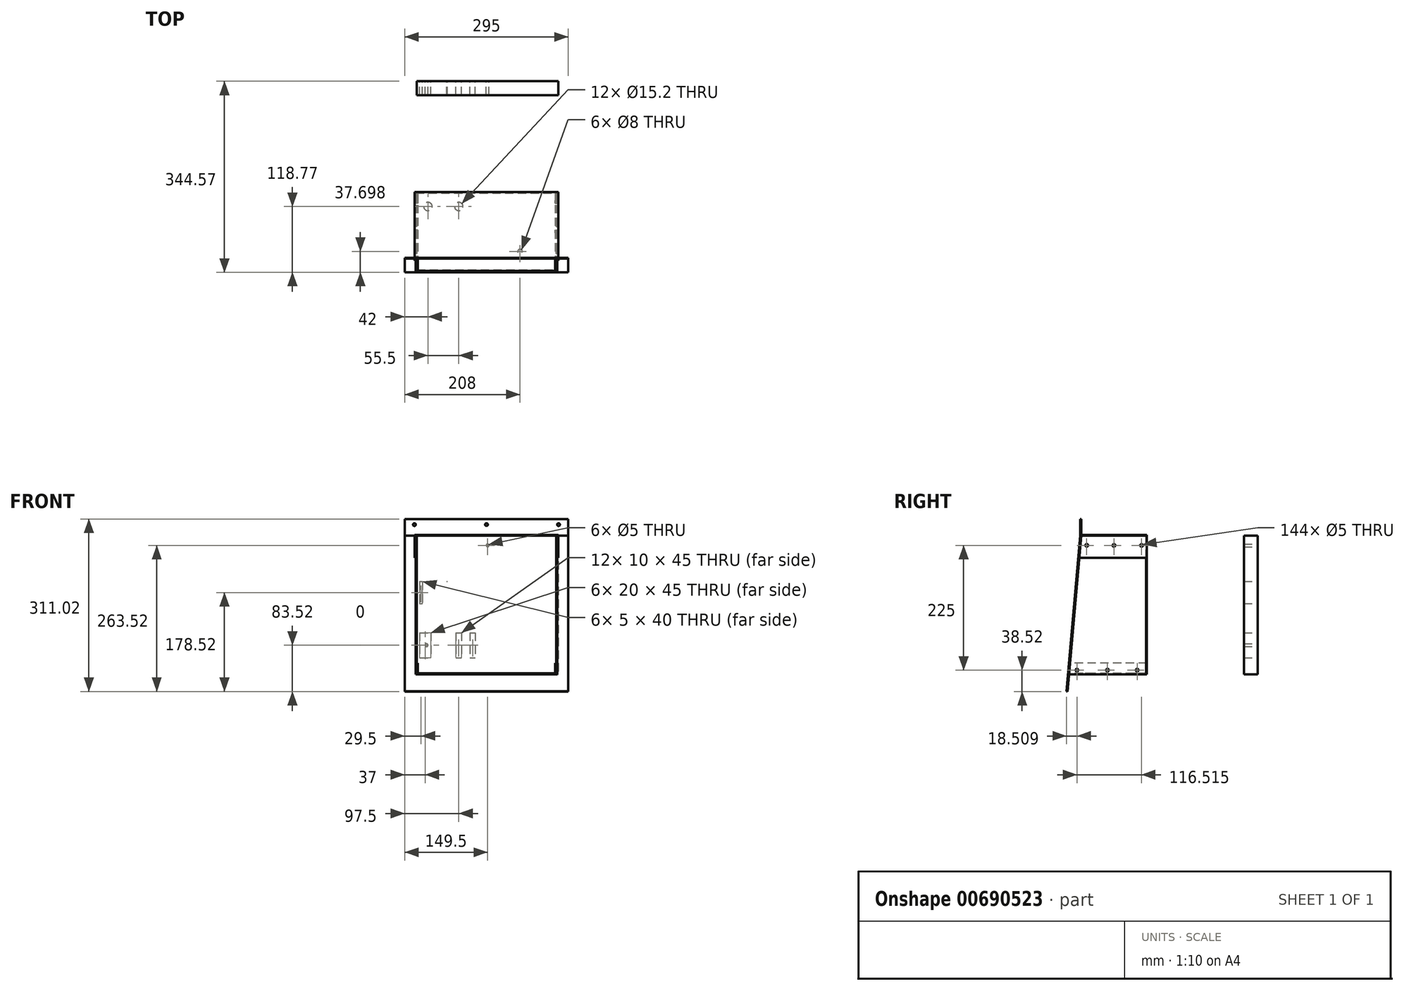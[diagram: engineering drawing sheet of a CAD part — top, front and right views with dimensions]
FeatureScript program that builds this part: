
annotation { "Feature Type Name" : "Feature", "Feature Type Description" : "" }
export const myFeature = defineFeature(function(context is Context, id is Id, definition is map)
    precondition{}
    {
        {
            var Q0;
            Q0=qCreatedBy(makeId("Right.planeOp"),FACE);
            var sketch = newSketch(context, id + "F0", { "sketchPlane" : qUnion([Q0])});
            skLineSegment(sketch, "E0.bottom", {"start": v(0, 0) * mm, "end": v(-141.87, 0) * mm});
            skLineSegment(sketch, "E0.top", {"start": v(0, 250) * mm, "end": v(-120, 250) * mm});
            skLineSegment(sketch, "E0.left", {"start": v(0, 0) * mm, "end": v(0, 250) * mm});
            skLineSegment(sketch, "E0.right", {"start": v(-141.87, 0) * mm, "end": v(-120, 250) * mm});
            skCircle(sketch, "E1", {"center": v(-17.5, 7.5) * mm, "radius": 2.5 * mm});
            skCircle(sketch, "E2", {"center": v(-70.94, 7.5) * mm, "radius": 2.5 * mm});
            skCircle(sketch, "E3", {"center": v(-126.06, 7.5) * mm, "radius": 2.5 * mm});
            skPoint(sketch, "E4", {"position": v(-70.94, 0) * mm});
            skCircle(sketch, "E5", {"center": v(-9.55, 232.5) * mm, "radius": 2.5 * mm});
            skCircle(sketch, "E6", {"center": v(-59.17, 232.5) * mm, "radius": 2.5 * mm});
            skCircle(sketch, "E7", {"center": v(-108.45, 232.5) * mm, "radius": 2.5 * mm});
            skSolve(sketch);
        }
        {
            var Q0;
            Q0 = qSketchRegion(id + "F0", true);
            extrude(context, id + "F1", {"entities" : qUnion([Q0]), "depth" : 1.6 * mm, "offsetDistance" : 25 * mm});
        }
        {
            var Q0;
            Q0=qCreatedBy(makeId("Front.planeOp"),FACE);
            var sketch = newSketch(context, id + "F2", { "sketchPlane" : qUnion([Q0])});
            skLineSegment(sketch, "E8.bottom", {"start": v(0, 0) * mm, "end": v(255, 0) * mm});
            skLineSegment(sketch, "E8.top", {"start": v(0, 250) * mm, "end": v(255, 250) * mm});
            skLineSegment(sketch, "E8.left", {"start": v(0, 0) * mm, "end": v(0, 250) * mm});
            skLineSegment(sketch, "E8.right", {"start": v(255, 0) * mm, "end": v(255, 250) * mm});
            skSolve(sketch);
        }
        {
            var Q0;
            Q0=makeQuery(id+"F2.imprint","IMPRINT",FACE,{"disambiguationData":[TD([[makeQuery(id+"F2.imprint","IMPRINT",EDGE,{"derivedFrom":sQuery(id+"F2.wireOp",EDGE,"E8.bottom")}),1.0]])]});
            var Q1;
            Q1 = qConstructionFilter(qBodyType(qCreatedBy(id + "F2" ,EDGE), BodyType.WIRE), ConstructionObject.NO);
            extrude(context, id + "F3", {"entities" : qUnion([Q0]), "surfaceEntities" : qUnion([Q1]), "depth" : 1.6 * mm, "offsetDistance" : 25 * mm});
        }
        {
            var Q0;
            Q0=qCreatedBy(makeId("Top.planeOp"),FACE);
            var sketch = newSketch(context, id + "F4", { "sketchPlane" : qUnion([Q0])});
            skLineSegment(sketch, "E9.bottom", {"start": v(2, 0) * mm, "end": v(253, 0) * mm});
            skLineSegment(sketch, "E9.top", {"start": v(2, -141.87) * mm, "end": v(253, -141.87) * mm});
            skLineSegment(sketch, "E9.left", {"start": v(2, 0) * mm, "end": v(2, -141.87) * mm});
            skLineSegment(sketch, "E9.right", {"start": v(253, 0) * mm, "end": v(253, -141.87) * mm});
            skCircle(sketch, "E10", {"center": v(22, -25.8) * mm, "radius": 7.6 * mm});
            skCircle(sketch, "E11", {"center": v(77.5, -25.8) * mm, "radius": 7.6 * mm});
            skCircle(sketch, "E12", {"center": v(188, -106.87) * mm, "radius": 4 * mm});
            skSolve(sketch);
        }
        {
            var Q0;
            Q0 = qSketchRegion(id + "F4", true);
            extrude(context, id + "F5", {"entities" : qUnion([Q0]), "depth" : 1.6 * mm, "offsetDistance" : 25 * mm});
        }
        {
            var Q0;
            Q0=sQuery(id+"F0.wireOp",EDGE,"E0.top");
            cPlane(context, id + "F6", {"entities" : qUnion([Q0]), "cplaneType" : CPlaneType.LINE_ANGLE, "offset" : 25 * mm, "angle" : 0 * degree, "width" : 150 * mm, "height" : 150 * mm});
        }
        {
            var Q0;
            Q0=qCreatedBy(id+"F6.planeOp",FACE);
            var sketch = newSketch(context, id + "F7", { "sketchPlane" : qUnion([Q0])});
            skLineSegment(sketch, "E13.bottom", {"start": v(-2, 0) * mm, "end": v(257, 0) * mm});
            skLineSegment(sketch, "E13.top", {"start": v(-2, 120) * mm, "end": v(257, 120) * mm});
            skLineSegment(sketch, "E13.left", {"start": v(-2, 0) * mm, "end": v(-2, 120) * mm});
            skLineSegment(sketch, "E13.right", {"start": v(257, 0) * mm, "end": v(257, 120) * mm});
            skSolve(sketch);
        }
        {
            var Q0;
            Q0 = qSketchRegion(id + "F7", true);
            extrude(context, id + "F8", {"entities" : qUnion([Q0]), "oppositeDirection" : true, "depth" : 1.6 * mm, "offsetDistance" : 25 * mm});
        }
        {
            var Q0;
            Q0=sQuery(id+"F2.wireOp",EDGE,"E8.right");
            cPlane(context, id + "F9", {"entities" : qUnion([Q0]), "cplaneType" : CPlaneType.LINE_ANGLE, "offset" : 25 * mm, "angle" : 0 * degree, "width" : 150 * mm, "height" : 150 * mm});
        }
        {
            var Q0;
            Q0=qCreatedBy(id+"F9.planeOp",FACE);
            var sketch = newSketch(context, id + "F10", { "sketchPlane" : qUnion([Q0])});
            skLineSegment(sketch, "E14.bottom", {"start": v(0, 0) * mm, "end": v(-141.87, 0) * mm});
            skLineSegment(sketch, "E14.top", {"start": v(0, 250) * mm, "end": v(-120, 250) * mm});
            skLineSegment(sketch, "E14.left", {"start": v(0, 0) * mm, "end": v(0, 250) * mm});
            skLineSegment(sketch, "E14.right", {"start": v(-141.87, 0) * mm, "end": v(-120, 250) * mm});
            skCircle(sketch, "E15", {"center": v(-126.06, 7.5) * mm, "radius": 2.5 * mm});
            skCircle(sketch, "E16", {"center": v(-70.94, 7.5) * mm, "radius": 2.5 * mm});
            skCircle(sketch, "E17", {"center": v(-17.5, 7.5) * mm, "radius": 2.5 * mm});
            skCircle(sketch, "E18", {"center": v(-9.55, 232.5) * mm, "radius": 2.5 * mm});
            skCircle(sketch, "E19", {"center": v(-59.17, 232.5) * mm, "radius": 2.5 * mm});
            skCircle(sketch, "E20", {"center": v(-108.45, 232.5) * mm, "radius": 2.5 * mm});
            skLineSegment(sketch, "E21", {"start": v(-141.87, 0) * mm, "end": v(-141.87, -30) * mm});
            skSolve(sketch);
        }
        {
            var Q0;
            Q0 = qSketchRegion(id + "F10", true);
            extrude(context, id + "F11", {"entities" : qUnion([Q0]), "oppositeDirection" : true, "depth" : 1.6 * mm, "offsetDistance" : 25 * mm});
        }
        {
            var Q0;
            Q0=sQuery(id+"F4.wireOp",EDGE,"E9.left");
            cPlane(context, id + "F12", {"entities" : qUnion([Q0]), "cplaneType" : CPlaneType.LINE_ANGLE, "offset" : 25 * mm, "angle" : 90 * degree, "width" : 150 * mm, "height" : 150 * mm});
        }
        {
            var Q0;
            Q0=qCreatedBy(id+"F12.planeOp",FACE);
            var sketch = newSketch(context, id + "F13", { "sketchPlane" : qUnion([Q0])});
            skLineSegment(sketch, "E22.bottom", {"start": v(0, 0) * mm, "end": v(-141.87, 0) * mm});
            skLineSegment(sketch, "E22.top", {"start": v(0, 20) * mm, "end": v(-140.12, 20) * mm});
            skLineSegment(sketch, "E22.left", {"start": v(0, 0) * mm, "end": v(0, 20) * mm});
            skLineSegment(sketch, "E22.right", {"start": v(-141.87, 0) * mm, "end": v(-140.12, 20) * mm});
            skCircle(sketch, "E23", {"center": v(-126.06, 7.5) * mm, "radius": 2.5 * mm});
            skCircle(sketch, "E24", {"center": v(-70.94, 7.5) * mm, "radius": 2.5 * mm});
            skCircle(sketch, "E25", {"center": v(-17.5, 7.5) * mm, "radius": 2.5 * mm});
            skPoint(sketch, "E26", {"position": v(-87.8, 0) * mm});
            skSolve(sketch);
        }
        {
            var Q0;
            Q0 = qSketchRegion(id + "F13", true);
            extrude(context, id + "F14", {"entities" : qUnion([Q0]), "depth" : 1.6 * mm, "offsetDistance" : 25 * mm});
        }
        {
            var Q0;
            Q0=sQuery(id+"F7.wireOp",EDGE,"E13.left");
            cPlane(context, id + "F15", {"entities" : qUnion([Q0]), "cplaneType" : CPlaneType.LINE_ANGLE, "offset" : 25 * mm, "angle" : 90 * degree, "width" : 150 * mm, "height" : 150 * mm});
        }
        {
            var Q0;
            Q0=qCreatedBy(id+"F15.planeOp",FACE);
            var sketch = newSketch(context, id + "F16", { "sketchPlane" : qUnion([Q0])});
            skLineSegment(sketch, "E27.bottom", {"start": v(0, 250) * mm, "end": v(-120, 250) * mm});
            skLineSegment(sketch, "E27.top", {"start": v(0, 210) * mm, "end": v(-123.5, 210) * mm});
            skLineSegment(sketch, "E27.left", {"start": v(0, 250) * mm, "end": v(0, 210) * mm});
            skLineSegment(sketch, "E27.right", {"start": v(-120, 250) * mm, "end": v(-123.5, 210) * mm});
            skCircle(sketch, "E28", {"center": v(-9.55, 232.5) * mm, "radius": 2.5 * mm});
            skCircle(sketch, "E29", {"center": v(-59.17, 232.5) * mm, "radius": 2.5 * mm});
            skCircle(sketch, "E30", {"center": v(-108.45, 232.5) * mm, "radius": 2.5 * mm});
            skSolve(sketch);
        }
        {
            var Q0;
            Q0 = qSketchRegion(id + "F16", true);
            extrude(context, id + "F17", {"entities" : qUnion([Q0]), "depth" : 1.6 * mm, "offsetDistance" : 25 * mm});
        }
        {
            var Q0;
            Q0=sQuery(id+"F7.wireOp",EDGE,"E13.right");
            cPlane(context, id + "F18", {"entities" : qUnion([Q0]), "cplaneType" : CPlaneType.LINE_ANGLE, "offset" : 25 * mm, "angle" : 90 * degree, "width" : 150 * mm, "height" : 150 * mm});
        }
        {
            var Q0;
            Q0=qCreatedBy(id+"F18.planeOp",FACE);
            var sketch = newSketch(context, id + "F19", { "sketchPlane" : qUnion([Q0])});
            skLineSegment(sketch, "E31.bottom", {"start": v(0, 250) * mm, "end": v(-120, 250) * mm});
            skLineSegment(sketch, "E31.top", {"start": v(0, 210) * mm, "end": v(-123.5, 210) * mm});
            skLineSegment(sketch, "E31.left", {"start": v(0, 250) * mm, "end": v(0, 210) * mm});
            skLineSegment(sketch, "E31.right", {"start": v(-120, 250) * mm, "end": v(-123.5, 210) * mm});
            skCircle(sketch, "E32", {"center": v(-108.45, 232.5) * mm, "radius": 2.5 * mm});
            skCircle(sketch, "E33", {"center": v(-59.17, 232.5) * mm, "radius": 2.5 * mm});
            skCircle(sketch, "E34", {"center": v(-9.55, 232.5) * mm, "radius": 2.5 * mm});
            skSolve(sketch);
        }
        {
            var Q0;
            Q0 = qSketchRegion(id + "F19", true);
            extrude(context, id + "F20", {"entities" : qUnion([Q0]), "oppositeDirection" : true, "depth" : 1.6 * mm, "offsetDistance" : 25 * mm});
        }
        {
            var Q0;
            Q0=sQuery(id+"F4.wireOp",EDGE,"E9.right");
            cPlane(context, id + "F21", {"entities" : qUnion([Q0]), "cplaneType" : CPlaneType.LINE_ANGLE, "offset" : 25 * mm, "angle" : 90 * degree, "width" : 150 * mm, "height" : 150 * mm});
        }
        {
            var Q0;
            Q0=qCreatedBy(id+"F21.planeOp",FACE);
            var sketch = newSketch(context, id + "F22", { "sketchPlane" : qUnion([Q0])});
            skLineSegment(sketch, "E35.bottom", {"start": v(0, 0) * mm, "end": v(-141.87, 0) * mm});
            skLineSegment(sketch, "E35.top", {"start": v(0, 20) * mm, "end": v(-140.12, 20) * mm});
            skLineSegment(sketch, "E35.left", {"start": v(0, 0) * mm, "end": v(0, 20) * mm});
            skLineSegment(sketch, "E35.right", {"start": v(-141.87, 0) * mm, "end": v(-140.12, 20) * mm});
            skCircle(sketch, "E36", {"center": v(-17.5, 7.5) * mm, "radius": 2.5 * mm});
            skCircle(sketch, "E37", {"center": v(-70.94, 7.5) * mm, "radius": 2.5 * mm});
            skCircle(sketch, "E38", {"center": v(-126.06, 7.5) * mm, "radius": 2.5 * mm});
            skSolve(sketch);
        }
        {
            var Q0;
            Q0 = qSketchRegion(id + "F22", true);
            extrude(context, id + "F23", {"entities" : qUnion([Q0]), "oppositeDirection" : true, "depth" : 1.6 * mm, "offsetDistance" : 25 * mm});
        }
        {
            var Q0;
            Q0=sQuery(id+"F0.wireOp",EDGE,"E0.right");
            cPlane(context, id + "F24", {"entities" : qUnion([Q0]), "cplaneType" : CPlaneType.LINE_ANGLE, "offset" : 25 * mm, "angle" : 90 * degree, "width" : 150 * mm, "height" : 150 * mm});
        }
        {
            var Q0;
            Q0=qCreatedBy(id+"F24.planeOp",FACE);
            var sketch = newSketch(context, id + "F25", { "sketchPlane" : qUnion([Q0])});
            skLineSegment(sketch, "E39.bottom", {"start": v(0, 238.59) * mm, "end": v(-255, 238.59) * mm});
            skLineSegment(sketch, "E39.top", {"start": v(0, -12.36) * mm, "end": v(-255, -12.36) * mm});
            skLineSegment(sketch, "E39.left", {"start": v(0, 238.59) * mm, "end": v(0, -12.36) * mm});
            skLineSegment(sketch, "E39.right", {"start": v(-255, 238.59) * mm, "end": v(-255, -12.36) * mm});
            skLineSegment(sketch, "E40.bottom", {"start": v(20, 238.59) * mm, "end": v(-275, 238.59) * mm});
            skLineSegment(sketch, "E40.top", {"start": v(20, -43.36) * mm, "end": v(-275, -43.36) * mm});
            skLineSegment(sketch, "E40.left", {"start": v(20, 238.59) * mm, "end": v(20, -43.36) * mm});
            skLineSegment(sketch, "E40.right", {"start": v(-275, 238.59) * mm, "end": v(-275, -43.36) * mm});
            skSolve(sketch);
        }
        {
            var Q0;
            Q0=makeQuery(id+"F2.imprint","IMPRINT",FACE,{"disambiguationData":[TD([[makeQuery(id+"F2.imprint","IMPRINT",EDGE,{"derivedFrom":sQuery(id+"F2.wireOp",EDGE,"E8.bottom")}),1.0]])]});
            cPlane(context, id + "F26", {"entities" : qUnion([Q0]), "cplaneType" : CPlaneType.OFFSET, "offset" : 200 * mm, "oppositeDirection" : true, "width" : 150 * mm, "height" : 150 * mm});
        }
        {
            var Q0;
            Q0=qCreatedBy(id+"F26.planeOp",FACE);
            var sketch = newSketch(context, id + "F27", { "sketchPlane" : qUnion([Q0])});
            skLineSegment(sketch, "E41.bottom", {"start": v(2, 250) * mm, "end": v(257, 250) * mm});
            skLineSegment(sketch, "E41.top", {"start": v(2, 0) * mm, "end": v(257, 0) * mm});
            skLineSegment(sketch, "E41.left", {"start": v(2, 250) * mm, "end": v(2, 0) * mm});
            skLineSegment(sketch, "E41.right", {"start": v(257, 250) * mm, "end": v(257, 0) * mm});
            skLineSegment(sketch, "E42.bottom", {"start": v(7, 245) * mm, "end": v(252, 245) * mm});
            skLineSegment(sketch, "E42.top", {"start": v(7, 5) * mm, "end": v(252, 5) * mm});
            skLineSegment(sketch, "E42.left", {"start": v(7, 245) * mm, "end": v(7, 5) * mm});
            skLineSegment(sketch, "E42.right", {"start": v(252, 245) * mm, "end": v(252, 5) * mm});
            skCircle(sketch, "E43", {"center": v(14.5, 12.5) * mm, "radius": 2.5 * mm});
            skCircle(sketch, "E44", {"center": v(129.5, 232.5) * mm, "radius": 2.5 * mm});
            skLineSegment(sketch, "E45.bottom", {"start": v(7, 75) * mm, "end": v(122.5, 75) * mm});
            skLineSegment(sketch, "E45.top", {"start": v(7, 30) * mm, "end": v(122.5, 30) * mm});
            skLineSegment(sketch, "E45.left", {"start": v(7, 75) * mm, "end": v(7, 30) * mm});
            skLineSegment(sketch, "E45.right", {"start": v(122.5, 75) * mm, "end": v(122.5, 30) * mm});
            skLineSegment(sketch, "E46.bottom", {"start": v(7, 167.5) * mm, "end": v(103, 167.5) * mm});
            skLineSegment(sketch, "E46.top", {"start": v(7, 127.5) * mm, "end": v(103, 127.5) * mm});
            skLineSegment(sketch, "E46.left", {"start": v(7, 167.5) * mm, "end": v(7, 127.5) * mm});
            skLineSegment(sketch, "E46.right", {"start": v(103, 167.5) * mm, "end": v(103, 127.5) * mm});
            skLineSegment(sketch, "E47.bottom", {"start": v(12, 190) * mm, "end": v(32, 190) * mm});
            skLineSegment(sketch, "E47.top", {"start": v(12, 105) * mm, "end": v(32, 105) * mm});
            skLineSegment(sketch, "E47.left", {"start": v(12, 190) * mm, "end": v(12, 105) * mm});
            skLineSegment(sketch, "E47.right", {"start": v(32, 190) * mm, "end": v(32, 105) * mm});
            skLineSegment(sketch, "E48.bottom", {"start": v(52, 196) * mm, "end": v(103, 196) * mm});
            skLineSegment(sketch, "E48.top", {"start": v(52, 105) * mm, "end": v(103, 105) * mm});
            skLineSegment(sketch, "E48.left", {"start": v(52, 196) * mm, "end": v(52, 105) * mm});
            skLineSegment(sketch, "E48.right", {"start": v(103, 196) * mm, "end": v(103, 105) * mm});
            skPoint(sketch, "E49", {"position": v(7, 52.5) * mm});
            skCircle(sketch, "E50", {"center": v(14.5, 147.5) * mm, "radius": 2.5 * mm});
            skPoint(sketch, "E51", {"position": v(7, 147.5) * mm});
            skLineSegment(sketch, "E52.bottom", {"start": v(152, 245) * mm, "end": v(252, 245) * mm});
            skLineSegment(sketch, "E52.top", {"start": v(152, 85) * mm, "end": v(252, 85) * mm});
            skLineSegment(sketch, "E52.left", {"start": v(152, 245) * mm, "end": v(152, 85) * mm});
            skLineSegment(sketch, "E52.right", {"start": v(252, 245) * mm, "end": v(252, 85) * mm});
            skCircle(sketch, "E53", {"center": v(202, 240) * mm, "radius": 2.5 * mm});
            skCircle(sketch, "E54", {"center": v(202, 90) * mm, "radius": 2.5 * mm});
            skPoint(sketch, "E55", {"position": v(202, 245) * mm});
            skLineSegment(sketch, "E56.bottom", {"start": v(56.85, 169.8) * mm, "end": v(98.15, 169.8) * mm});
            skLineSegment(sketch, "E56.top", {"start": v(56.85, 131.2) * mm, "end": v(98.15, 131.2) * mm});
            skLineSegment(sketch, "E56.left", {"start": v(56.85, 169.8) * mm, "end": v(56.85, 131.2) * mm});
            skLineSegment(sketch, "E56.right", {"start": v(98.15, 169.8) * mm, "end": v(98.15, 131.2) * mm});
            skPoint(sketch, "E57", {"position": v(77.5, 196) * mm});
            skPoint(sketch, "E58", {"position": v(77.5, 169.8) * mm});
            skPoint(sketch, "E59", {"position": v(98.15, 150.5) * mm});
            skPoint(sketch, "E60", {"position": v(103, 150.5) * mm});
            skCircle(sketch, "E61", {"center": v(56.85, 169.8) * mm, "radius": 2.5 * mm});
            skCircle(sketch, "E62", {"center": v(98.15, 169.8) * mm, "radius": 2.5 * mm});
            skCircle(sketch, "E63", {"center": v(98.15, 131.2) * mm, "radius": 2.5 * mm});
            skCircle(sketch, "E64", {"center": v(56.85, 131.2) * mm, "radius": 2.5 * mm});
            skLineSegment(sketch, "E65.bottom", {"start": v(17, 75) * mm, "end": v(27, 75) * mm});
            skLineSegment(sketch, "E65.top", {"start": v(17, 30) * mm, "end": v(27, 30) * mm});
            skLineSegment(sketch, "E65.left", {"start": v(17, 75) * mm, "end": v(17, 30) * mm});
            skLineSegment(sketch, "E65.right", {"start": v(27, 75) * mm, "end": v(27, 30) * mm});
            skPoint(sketch, "E66", {"position": v(22, 75) * mm});
            skPoint(sketch, "E67", {"position": v(22, 105) * mm});
            skPoint(sketch, "E68", {"position": v(12, 147.5) * mm});
            skPoint(sketch, "E69", {"position": v(77.5, 105) * mm});
            skLineSegment(sketch, "E70.bottom", {"start": v(72.5, 75) * mm, "end": v(82.5, 75) * mm});
            skLineSegment(sketch, "E70.top", {"start": v(72.5, 30) * mm, "end": v(82.5, 30) * mm});
            skLineSegment(sketch, "E70.left", {"start": v(72.5, 75) * mm, "end": v(72.5, 30) * mm});
            skLineSegment(sketch, "E70.right", {"start": v(82.5, 75) * mm, "end": v(82.5, 30) * mm});
            skPoint(sketch, "E71", {"position": v(77.5, 75) * mm});
            skLineSegment(sketch, "E72.bottom", {"start": v(97.5, 75) * mm, "end": v(107.5, 75) * mm});
            skLineSegment(sketch, "E72.top", {"start": v(97.5, 30) * mm, "end": v(107.5, 30) * mm});
            skLineSegment(sketch, "E72.left", {"start": v(97.5, 75) * mm, "end": v(97.5, 30) * mm});
            skLineSegment(sketch, "E72.right", {"start": v(107.5, 75) * mm, "end": v(107.5, 30) * mm});
            skPoint(sketch, "E73", {"position": v(32, 147.5) * mm});
            skCircle(sketch, "E74", {"center": v(34.5, 147.5) * mm, "radius": 2.5 * mm});
            skCircle(sketch, "E75", {"center": v(90.5, 147.5) * mm, "radius": 2.5 * mm});
            skCircle(sketch, "E76", {"center": v(19.5, 52.5) * mm, "radius": 2.5 * mm});
            skCircle(sketch, "E77", {"center": v(110, 52.5) * mm, "radius": 2.5 * mm});
            skCircle(sketch, "E78", {"center": v(14.5, 232.5) * mm, "radius": 2.5 * mm});
            skCircle(sketch, "E79", {"center": v(239.5, 12.5) * mm, "radius": 2.5 * mm});
            skSolve(sketch);
        }
        {
            var Q0;
            {var subQ0=sQuery(id+"F27.wireOp",EDGE,"E74");Q0=makeQuery(id+"F27.imprint","IMPRINT",FACE,{"disambiguationData":[TD([[makeQuery(id+"F27.imprint","IMPRINT",EDGE,{"derivedFrom":subQ0}),-1.0]])]});}
            var Q1;
            {var subQ0=sQuery(id+"F27.wireOp",EDGE,"E65.right");Q1=makeQuery(id+"F27.imprint","IMPRINT",FACE,{"disambiguationData":[TD([[makeQuery(id+"F27.imprint","IMPRINT",EDGE,{"derivedFrom":subQ0}),1.0]])]});}
            var Q2;
            {var subQ0=sQuery(id+"F27.wireOp",EDGE,"E70.right");Q2=makeQuery(id+"F27.imprint","IMPRINT",FACE,{"disambiguationData":[TD([[makeQuery(id+"F27.imprint","IMPRINT",EDGE,{"derivedFrom":subQ0}),1.0]])]});}
            var Q3;
            Q3=makeQuery(id+"F27.imprint","IMPRINT",FACE,{"disambiguationData":[TD([[makeQuery(id+"F27.imprint","IMPRINT",EDGE,{"derivedFrom":sQuery(id+"F27.wireOp",EDGE,"E52.bottom")}),-1.0]])]});
            var Q4;
            {var subQ5=sQuery(id+"F27.wireOp",EDGE,"E48.top");Q4=makeQuery(id+"F27.imprint","IMPRINT",FACE,{"disambiguationData":[TD([[makeQuery(id+"F27.imprint","IMPRINT",EDGE,{"derivedFrom":subQ5}),1.0]])]});}
            var Q5;
            {var subQ1=sQuery(id+"F27.wireOp",EDGE,"E48.bottom");Q5=makeQuery(id+"F27.imprint","IMPRINT",FACE,{"disambiguationData":[TD([[makeQuery(id+"F27.imprint","IMPRINT",EDGE,{"derivedFrom":subQ1}),-1.0]])]});}
            var Q6;
            {var subQ5=sQuery(id+"F27.wireOp",EDGE,"E47.bottom");Q6=makeQuery(id+"F27.imprint","IMPRINT",FACE,{"disambiguationData":[TD([[makeQuery(id+"F27.imprint","IMPRINT",EDGE,{"derivedFrom":subQ5}),-1.0]])]});}
            var Q7;
            {var subQ5=sQuery(id+"F27.wireOp",EDGE,"E47.top");Q7=makeQuery(id+"F27.imprint","IMPRINT",FACE,{"disambiguationData":[TD([[makeQuery(id+"F27.imprint","IMPRINT",EDGE,{"derivedFrom":subQ5}),1.0]])]});}
            var Q8;
            Q8=makeQuery(id+"F27.imprint","IMPRINT",FACE,{"disambiguationData":[TD([[makeQuery(id+"F27.imprint","IMPRINT",EDGE,{"derivedFrom":sQuery(id+"F27.wireOp",EDGE,"E75")}),-1.0]])]});
            var Q9;
            Q9=makeQuery(id+"F27.imprint","IMPRINT",FACE,{"disambiguationData":[TD([[makeQuery(id+"F27.imprint","IMPRINT",EDGE,{"derivedFrom":sQuery(id+"F27.wireOp",EDGE,"E70.bottom")}),-1.0]])]});
            var Q10;
            {var subQ33=sQuery(id+"F27.wireOp",EDGE,"E42.bottom");Q10=makeQuery(id+"F27.imprint","IMPRINT",FACE,{"disambiguationData":[TD([[makeQuery(id+"F27.imprint","IMPRINT",EDGE,{"derivedFrom":subQ33}),-1.0]])]});}
            var Q11;
            {var subQ1=sQuery(id+"F27.wireOp",EDGE,"E72.bottom");Q11=makeQuery(id+"F27.imprint","IMPRINT",FACE,{"disambiguationData":[TD([[makeQuery(id+"F27.imprint","IMPRINT",EDGE,{"derivedFrom":subQ1}),-1.0]])]});}
            var Q12;
            Q12=makeQuery(id+"F27.imprint","IMPRINT",FACE,{"disambiguationData":[TD([[makeQuery(id+"F27.imprint","IMPRINT",EDGE,{"derivedFrom":sQuery(id+"F27.wireOp",EDGE,"E41.bottom")}),-1.0]])]});
            var Q13;
            {var subQ4=sQuery(id+"F27.wireOp",EDGE,"E45.left");Q13=makeQuery(id+"F27.imprint","IMPRINT",FACE,{"disambiguationData":[TD([[makeQuery(id+"F27.imprint","IMPRINT",EDGE,{"derivedFrom":subQ4}),1.0]])]});}
            var Q14;
            {var subQ0=sQuery(id+"F27.wireOp",EDGE,"E61");var subQ1=sQuery(id+"F27.wireOp",EDGE,"E46.bottom");var subQ2=makeQuery(id+"F27.imprint","INTERSECT",VERTEX,{"disambiguationData":[OD(1.0)],"derivedFrom":[subQ1,subQ0]});Q14=makeQuery(id+"F27.imprint","IMPRINT",FACE,{"disambiguationData":[TD([[makeQuery(id+"F27.imprint","IMPRINT",EDGE,{"disambiguationData":[TD([[subQ2,-1.0]])],"derivedFrom":subQ1}),1.0]])]});}
            var Q15;
            {var subQ0=sQuery(id+"F27.wireOp",EDGE,"E45.right");Q15=makeQuery(id+"F27.imprint","IMPRINT",FACE,{"disambiguationData":[TD([[makeQuery(id+"F27.imprint","IMPRINT",EDGE,{"derivedFrom":subQ0}),-1.0]])]});}
            var Q16;
            {var subQ0=sQuery(id+"F27.wireOp",EDGE,"E50");Q16=makeQuery(id+"F27.imprint","IMPRINT",FACE,{"disambiguationData":[TD([[makeQuery(id+"F27.imprint","IMPRINT",EDGE,{"derivedFrom":subQ0}),-1.0]])]});}
            var Q17;
            {var subQ1=sQuery(id+"F27.wireOp",EDGE,"E46.bottom");var subQ18=sQuery(id+"F27.wireOp",EDGE,"E48.left");var subQ19=makeQuery(id+"F27.imprint","INTERSECT",VERTEX,{"derivedFrom":[subQ1,subQ18]});Q17=makeQuery(id+"F27.imprint","IMPRINT",FACE,{"disambiguationData":[TD([[makeQuery(id+"F27.imprint","IMPRINT",EDGE,{"disambiguationData":[TD([[subQ19,-1.0]])],"derivedFrom":subQ1}),-1.0]])]});}
            var Q18;
            {var subQ4=sQuery(id+"F27.wireOp",EDGE,"E65.bottom");Q18=makeQuery(id+"F27.imprint","IMPRINT",FACE,{"disambiguationData":[TD([[makeQuery(id+"F27.imprint","IMPRINT",EDGE,{"derivedFrom":subQ4}),-1.0]])]});}
            var Q19;
            {var subQ4=sQuery(id+"F27.wireOp",EDGE,"E46.left");Q19=makeQuery(id+"F27.imprint","IMPRINT",FACE,{"disambiguationData":[TD([[makeQuery(id+"F27.imprint","IMPRINT",EDGE,{"derivedFrom":subQ4}),1.0]])]});}
            var Q20;
            Q20=makeQuery(id+"F27.imprint","IMPRINT",FACE,{"disambiguationData":[TD([[makeQuery(id+"F27.imprint","IMPRINT",EDGE,{"derivedFrom":sQuery(id+"F27.wireOp",EDGE,"E44")}),-1.0]])]});
            var Q21;
            Q21=makeQuery(id+"F27.imprint","IMPRINT",FACE,{"disambiguationData":[TD([[makeQuery(id+"F27.imprint","IMPRINT",EDGE,{"derivedFrom":sQuery(id+"F27.wireOp",EDGE,"E54")}),1.0]])]});
            var Q22;
            Q22=makeQuery(id+"F27.imprint","IMPRINT",FACE,{"disambiguationData":[TD([[makeQuery(id+"F27.imprint","IMPRINT",EDGE,{"derivedFrom":sQuery(id+"F27.wireOp",EDGE,"E77")}),1.0]])]});
            var Q23;
            Q23=makeQuery(id+"F27.imprint","IMPRINT",FACE,{"disambiguationData":[TD([[makeQuery(id+"F27.imprint","IMPRINT",EDGE,{"derivedFrom":sQuery(id+"F27.wireOp",EDGE,"E78")}),1.0]])]});
            var Q24;
            Q24=makeQuery(id+"F27.imprint","IMPRINT",FACE,{"disambiguationData":[TD([[makeQuery(id+"F27.imprint","IMPRINT",EDGE,{"derivedFrom":sQuery(id+"F27.wireOp",EDGE,"E79")}),1.0]])]});
            var Q25;
            Q25=makeQuery(id+"F27.imprint","IMPRINT",FACE,{"disambiguationData":[TD([[makeQuery(id+"F27.imprint","IMPRINT",EDGE,{"derivedFrom":sQuery(id+"F27.wireOp",EDGE,"E43")}),1.0]])]});
            var Q26;
            Q26=makeQuery(id+"F27.imprint","IMPRINT",FACE,{"disambiguationData":[TD([[makeQuery(id+"F27.imprint","IMPRINT",EDGE,{"derivedFrom":sQuery(id+"F27.wireOp",EDGE,"E50")}),1.0]])]});
            var Q27;
            Q27=makeQuery(id+"F27.imprint","IMPRINT",FACE,{"disambiguationData":[TD([[makeQuery(id+"F27.imprint","IMPRINT",EDGE,{"derivedFrom":sQuery(id+"F27.wireOp",EDGE,"E53")}),1.0]])]});
            var Q28;
            Q28=makeQuery(id+"F27.imprint","IMPRINT",FACE,{"disambiguationData":[TD([[makeQuery(id+"F27.imprint","IMPRINT",EDGE,{"derivedFrom":sQuery(id+"F27.wireOp",EDGE,"E74")}),1.0]])]});
            var Q29;
            Q29=makeQuery(id+"F27.imprint","IMPRINT",FACE,{"disambiguationData":[TD([[makeQuery(id+"F27.imprint","IMPRINT",EDGE,{"derivedFrom":sQuery(id+"F27.wireOp",EDGE,"E75")}),1.0]])]});
            var Q30;
            Q30=makeQuery(id+"F27.imprint","IMPRINT",FACE,{"disambiguationData":[TD([[makeQuery(id+"F27.imprint","IMPRINT",EDGE,{"derivedFrom":sQuery(id+"F27.wireOp",EDGE,"E76")}),1.0]])]});
            var Q31;
            {var subQ0=sQuery(id+"F27.wireOp",EDGE,"E56.right");var subQ1=sQuery(id+"F27.wireOp",EDGE,"E56.top");var subQ2=makeQuery(id+"F27.imprint","INTERSECT",VERTEX,{"derivedFrom":[subQ1,subQ0]});Q31=makeQuery(id+"F27.imprint","IMPRINT",FACE,{"disambiguationData":[TD([[makeQuery(id+"F27.imprint","IMPRINT",EDGE,{"disambiguationData":[TD([[subQ2,1.0]])],"derivedFrom":subQ1}),-1.0]])]});}
            var Q32;
            {var subQ0=sQuery(id+"F27.wireOp",EDGE,"E56.left");var subQ1=sQuery(id+"F27.wireOp",EDGE,"E56.top");var subQ2=makeQuery(id+"F27.imprint","INTERSECT",VERTEX,{"derivedFrom":[subQ1,subQ0]});Q32=makeQuery(id+"F27.imprint","IMPRINT",FACE,{"disambiguationData":[TD([[makeQuery(id+"F27.imprint","IMPRINT",EDGE,{"disambiguationData":[TD([[subQ2,-1.0]])],"derivedFrom":subQ1}),-1.0]])]});}
            var Q33;
            {var subQ0=sQuery(id+"F27.wireOp",EDGE,"E56.left");var subQ1=sQuery(id+"F27.wireOp",EDGE,"E56.top");var subQ2=makeQuery(id+"F27.imprint","INTERSECT",VERTEX,{"derivedFrom":[subQ1,subQ0]});Q33=makeQuery(id+"F27.imprint","IMPRINT",FACE,{"disambiguationData":[TD([[makeQuery(id+"F27.imprint","IMPRINT",EDGE,{"disambiguationData":[TD([[subQ2,-1.0]])],"derivedFrom":subQ1}),1.0]])]});}
            var Q34;
            {var subQ0=sQuery(id+"F27.wireOp",EDGE,"E61");var subQ1=sQuery(id+"F27.wireOp",EDGE,"E46.bottom");var subQ2=makeQuery(id+"F27.imprint","INTERSECT",VERTEX,{"disambiguationData":[OD(0.0)],"derivedFrom":[subQ1,subQ0]});Q34=makeQuery(id+"F27.imprint","IMPRINT",FACE,{"disambiguationData":[TD([[makeQuery(id+"F27.imprint","IMPRINT",EDGE,{"disambiguationData":[TD([[subQ2,-1.0]])],"derivedFrom":subQ1}),1.0]])]});}
            var Q35;
            {var subQ0=sQuery(id+"F27.wireOp",EDGE,"E56.left");var subQ1=sQuery(id+"F27.wireOp",EDGE,"E46.bottom");var subQ2=makeQuery(id+"F27.imprint","INTERSECT",VERTEX,{"derivedFrom":[subQ1,subQ0]});Q35=makeQuery(id+"F27.imprint","IMPRINT",FACE,{"disambiguationData":[TD([[makeQuery(id+"F27.imprint","IMPRINT",EDGE,{"disambiguationData":[TD([[subQ2,-1.0]])],"derivedFrom":subQ1}),1.0]])]});}
            var Q36;
            {var subQ0=sQuery(id+"F27.wireOp",EDGE,"E56.left");var subQ1=sQuery(id+"F27.wireOp",EDGE,"E46.bottom");var subQ2=makeQuery(id+"F27.imprint","INTERSECT",VERTEX,{"derivedFrom":[subQ1,subQ0]});Q36=makeQuery(id+"F27.imprint","IMPRINT",FACE,{"disambiguationData":[TD([[makeQuery(id+"F27.imprint","IMPRINT",EDGE,{"disambiguationData":[TD([[subQ2,-1.0]])],"derivedFrom":subQ1}),-1.0]])]});}
            var Q37;
            {var subQ0=sQuery(id+"F27.wireOp",EDGE,"E62");var subQ1=sQuery(id+"F27.wireOp",EDGE,"E46.bottom");var subQ2=makeQuery(id+"F27.imprint","INTERSECT",VERTEX,{"disambiguationData":[OD(0.0)],"derivedFrom":[subQ1,subQ0]});Q37=makeQuery(id+"F27.imprint","IMPRINT",FACE,{"disambiguationData":[TD([[makeQuery(id+"F27.imprint","IMPRINT",EDGE,{"disambiguationData":[TD([[subQ2,-1.0]])],"derivedFrom":subQ1}),1.0]])]});}
            var Q38;
            {var subQ0=sQuery(id+"F27.wireOp",EDGE,"E56.right");var subQ1=sQuery(id+"F27.wireOp",EDGE,"E46.bottom");var subQ2=makeQuery(id+"F27.imprint","INTERSECT",VERTEX,{"derivedFrom":[subQ1,subQ0]});Q38=makeQuery(id+"F27.imprint","IMPRINT",FACE,{"disambiguationData":[TD([[makeQuery(id+"F27.imprint","IMPRINT",EDGE,{"disambiguationData":[TD([[subQ2,-1.0]])],"derivedFrom":subQ1}),1.0]])]});}
            var Q39;
            {var subQ0=sQuery(id+"F27.wireOp",EDGE,"E61");var subQ1=sQuery(id+"F27.wireOp",EDGE,"E46.bottom");var subQ2=makeQuery(id+"F27.imprint","INTERSECT",VERTEX,{"disambiguationData":[OD(0.0)],"derivedFrom":[subQ1,subQ0]});Q39=makeQuery(id+"F27.imprint","IMPRINT",FACE,{"disambiguationData":[TD([[makeQuery(id+"F27.imprint","IMPRINT",EDGE,{"disambiguationData":[TD([[subQ2,-1.0]])],"derivedFrom":subQ1}),-1.0]])]});}
            var Q40;
            {var subQ0=sQuery(id+"F27.wireOp",EDGE,"E56.right");var subQ1=sQuery(id+"F27.wireOp",EDGE,"E46.bottom");var subQ2=makeQuery(id+"F27.imprint","INTERSECT",VERTEX,{"derivedFrom":[subQ1,subQ0]});Q40=makeQuery(id+"F27.imprint","IMPRINT",FACE,{"disambiguationData":[TD([[makeQuery(id+"F27.imprint","IMPRINT",EDGE,{"disambiguationData":[TD([[subQ2,-1.0]])],"derivedFrom":subQ1}),-1.0]])]});}
            var Q41;
            {var subQ0=sQuery(id+"F27.wireOp",EDGE,"E56.right");var subQ1=sQuery(id+"F27.wireOp",EDGE,"E56.top");var subQ2=makeQuery(id+"F27.imprint","INTERSECT",VERTEX,{"derivedFrom":[subQ1,subQ0]});Q41=makeQuery(id+"F27.imprint","IMPRINT",FACE,{"disambiguationData":[TD([[makeQuery(id+"F27.imprint","IMPRINT",EDGE,{"disambiguationData":[TD([[subQ2,1.0]])],"derivedFrom":subQ1}),1.0]])]});}
            var Q42;
            {var subQ0=sQuery(id+"F27.wireOp",EDGE,"E62");var subQ1=sQuery(id+"F27.wireOp",EDGE,"E46.bottom");var subQ2=makeQuery(id+"F27.imprint","INTERSECT",VERTEX,{"disambiguationData":[OD(0.0)],"derivedFrom":[subQ1,subQ0]});Q42=makeQuery(id+"F27.imprint","IMPRINT",FACE,{"disambiguationData":[TD([[makeQuery(id+"F27.imprint","IMPRINT",EDGE,{"disambiguationData":[TD([[subQ2,-1.0]])],"derivedFrom":subQ1}),-1.0]])]});}
            extrude(context, id + "F28", {"entities" : qUnion([Q0, Q1, Q2, Q3, Q4, Q5, Q6, Q7, Q8, Q9, Q10, Q11, Q12, Q13, Q14, Q15, Q16, Q17, Q18, Q19, Q20, Q21, Q22, Q23, Q24, Q25, Q26, Q27, Q28, Q29, Q30, Q31, Q32, Q33, Q34, Q35, Q36, Q37, Q38, Q39, Q40, Q41, Q42]), "depth" : 25 * mm, "offsetDistance" : 25 * mm});
        }
        {
            var Q0;
            Q0=sQuery(id+"F7.wireOp",EDGE,"E13.top");
            cPlane(context, id + "F29", {"entities" : qUnion([Q0]), "cplaneType" : CPlaneType.LINE_ANGLE, "offset" : 25 * mm, "angle" : 0 * degree, "width" : 150 * mm, "height" : 150 * mm});
        }
        {
            var Q0;
            Q0=qCreatedBy(id+"F29.planeOp",FACE);
            var sketch = newSketch(context, id + "F30", { "sketchPlane" : qUnion([Q0])});
            skLineSegment(sketch, "E80.bottom", {"start": v(20, 280) * mm, "end": v(-275, 280) * mm});
            skLineSegment(sketch, "E80.top", {"start": v(20, 250) * mm, "end": v(-275, 250) * mm});
            skLineSegment(sketch, "E80.left", {"start": v(20, 280) * mm, "end": v(20, 250) * mm});
            skLineSegment(sketch, "E80.right", {"start": v(-275, 280) * mm, "end": v(-275, 250) * mm});
            skPoint(sketch, "E81", {"position": v(-127.5, 280) * mm});
            skPoint(sketch, "E82", {"position": v(-275, 270) * mm});
            skCircle(sketch, "E83", {"center": v(-257.5, 270) * mm, "radius": 2.5 * mm});
            skCircle(sketch, "E84", {"center": v(-127.5, 270) * mm, "radius": 2.5 * mm});
            skCircle(sketch, "E85", {"center": v(2.5, 270) * mm, "radius": 2.5 * mm});
            skSolve(sketch);
        }
        {
            var Q0;
            Q0=makeQuery(id+"F25.imprint","IMPRINT",FACE,{"disambiguationData":[TD([[makeQuery(id+"F25.imprint","IMPRINT",EDGE,{"derivedFrom":sQuery(id+"F25.wireOp",EDGE,"E39.top")}),1.0]])]});
            var Q1;
            Q1=makeQuery(id+"F30.imprint","IMPRINT",FACE,{"disambiguationData":[TD([[makeQuery(id+"F30.imprint","IMPRINT",EDGE,{"derivedFrom":sQuery(id+"F30.wireOp",EDGE,"E80.bottom")}),1.0]])]});
            extrude(context, id + "F31", {"entities" : qUnion([Q0, Q1]), "depth" : 1.6 * mm, "offsetDistance" : 25 * mm});
        }
    });
